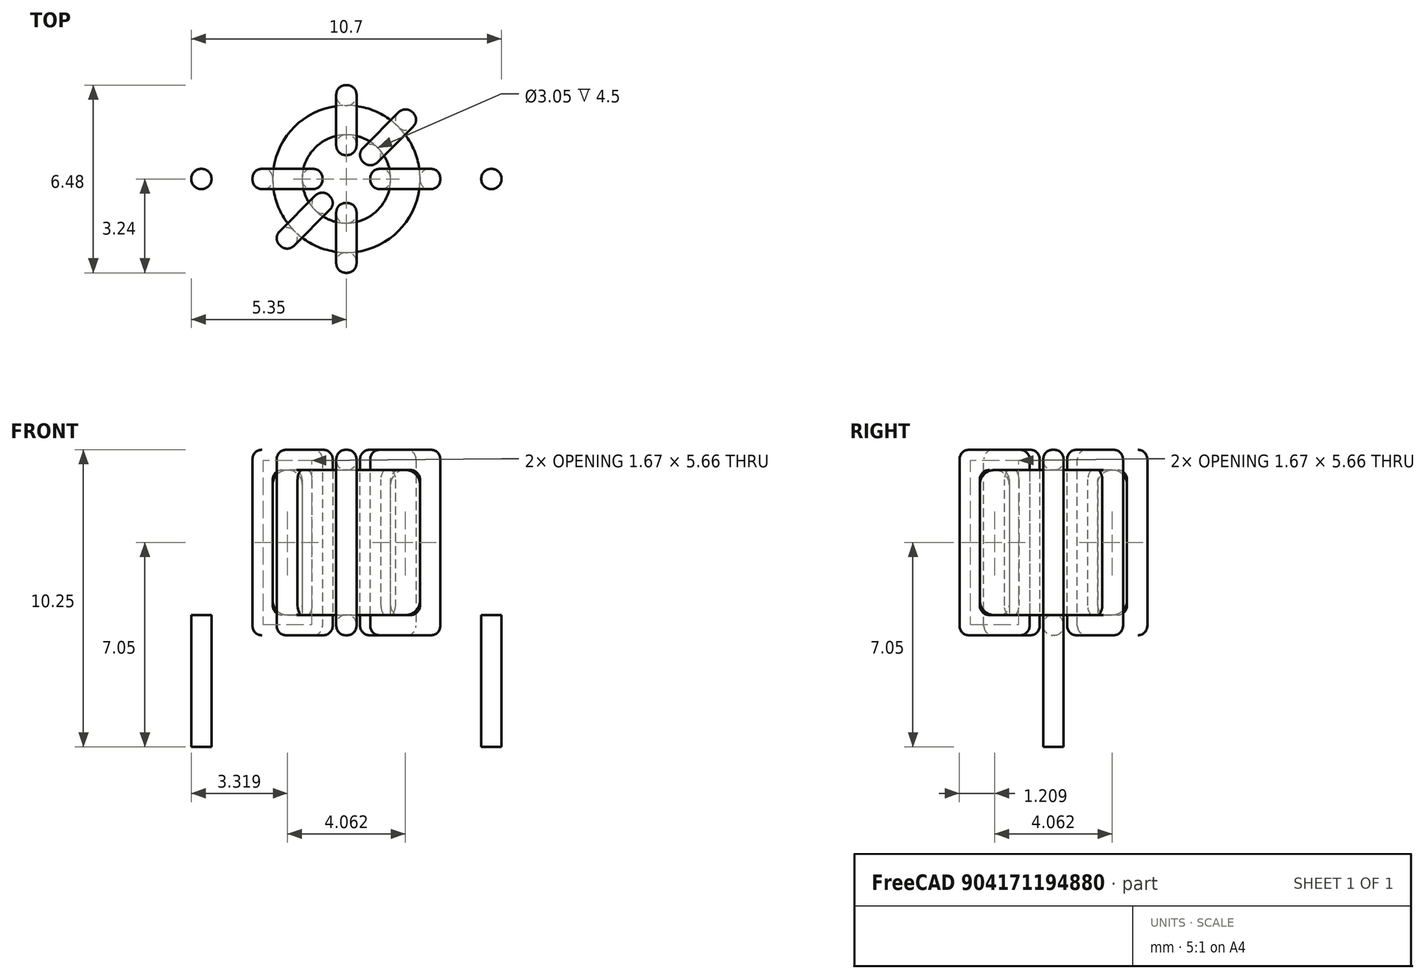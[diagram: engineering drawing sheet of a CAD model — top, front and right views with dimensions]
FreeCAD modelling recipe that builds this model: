
FCSTD DOCUMENT  (FreeCAD 0.16R6703 (Git))
Label: L_Toroid_Horizontal_D6.5mm_P10.00mm_Diameter7-5mm_Amidon-T25
License: All rights reserved
LicenseURL: http://en.wikipedia.org/wiki/All_rights_reserved
objects: Sketcher::SketchObject×6, PartDesign::Pad×6, PartDesign::Fillet×5, Spreadsheet::Sheet×1
note: 23 computed .brp shape members not serialized (recipe doc carries the construction recipe); baked Part::Feature solids carry a one-line shape summary decoded from their .brp

FEATURE [Spreadsheet::Sheet] Spreadsheet  label="dimensions"
  cells = A1=Wx; B1(Wx)=6.476999999999999; C1(WW)=3.048; D1=6.476999999999999; A2=Wy; B2(Wy)=6.476999999999999; D2=6.476999999999999; A3=RM; B3(RMx)=10; C3(RMy)=0; A4=d_wire; B4(d_wire)=0.7; A5=H; B5(H)=5; A6=offsetx; B6(offsetx)=-1.7615
FEATURE [Sketcher::SketchObject] Sketch
  Placement = pos=(0,0,1.2) rot=(0,0,1;0rad)
  expr: Placement.Base.z = 0.5 + Spreadsheet.d_wire
  expr: Constraints[0] = Spreadsheet.Wx / 2 - Spreadsheet.d_wire
  expr: Constraints[4] = Spreadsheet.WW / 2
  expr: Constraints[2] = Spreadsheet.RMy / 2
  expr: Constraints[1] = Spreadsheet.RMx / 2
  sketch-geometry (2):
    g0: Circle CenterX=5 CenterY=0 CenterZ=0 NormalX=0 NormalY=0 NormalZ=1 Radius=2.5385
    g1: Circle CenterX=5 CenterY=0 CenterZ=0 NormalX=0 NormalY=0 NormalZ=1 Radius=1.524
  constraints (5):
    c: Radius(g0) = 2.5385
    c: DistanceX(g-1,g0) = 5
    c: DistanceY(g-1,g0) = 0
    c: Coincident(g1,g0)
    c: Radius(g1) = 1.524
FEATURE [PartDesign::Pad] Pad
  Length = 5
  Length2 = 100
  Placement = pos=(0,0,1.2) rot=(0,0,1;0rad)
  Sketch = -> Sketch
  Type = 0
  expr: Length = Spreadsheet.H
FEATURE [Sketcher::SketchObject] Sketch001
  Placement = pos=(0,0,0.85) rot=(0,0,1;0rad)
  expr: Placement.Base.z = 0.5 + Spreadsheet.d_wire * 0.5
  expr: Constraints[4] = Spreadsheet.RMx
  expr: Constraints[2] = Spreadsheet.RMy
  expr: Constraints[1] = Spreadsheet.d_wire / 2
  sketch-geometry (2):
    g0: Circle CenterX=0 CenterY=0 CenterZ=0 NormalX=0 NormalY=0 NormalZ=1 Radius=0.35
    g1: Circle CenterX=10 CenterY=0 CenterZ=0 NormalX=0 NormalY=0 NormalZ=1 Radius=0.35
  constraints (5):
    c: Equal(g0,g1)
    c: Radius(g0) = 0.35
    c: DistanceY(g-1,g1) = 0
    c: Coincident(g0,g-1)
    c: DistanceX(g-1,g1) = 10
FEATURE [PartDesign::Pad] Pad001
  Length = 0.35
  Length2 = 4.2
  Placement = pos=(0,0,0.85) rot=(0,0,1;0rad)
  Reversed = true
  Sketch = -> Sketch001
  Type = 4
  expr: Length2 = 3.5 + Spreadsheet.d_wire
  expr: Length = Spreadsheet.d_wire / 2
FEATURE [PartDesign::Fillet] Fillet
  Base = -> Pad [Edge6,Edge3,Edge2]
  Placement = pos=(0,0,1.2) rot=(0,0,1;0rad)
  Radius = 0.5
FEATURE [Sketcher::SketchObject] Sketch003
  Placement = pos=(5,0,0) rot=(1,0,0;1.5708rad)
  expr: Placement.Base.x = Spreadsheet.RMx / 2
  expr: Constraints[49] = Spreadsheet.Wx - Spreadsheet.d_wire * 2
  expr: Constraints[44] = Spreadsheet.d_wire
  expr: Constraints[23] = Spreadsheet.H
  expr: Constraints[22] = Spreadsheet.Wx / 2 - Spreadsheet.d_wire
  expr: Placement.Base.y = Spreadsheet.RMy / 2
  expr: Constraints[21] = (Spreadsheet.Wx - Spreadsheet.WW) / 2 - Spreadsheet.d_wire
  expr: Constraints[19] = Spreadsheet.d_wire
  expr: Constraints[17] = Spreadsheet.d_wire
  expr: Constraints[18] = Spreadsheet.d_wire
  expr: Constraints[16] = Spreadsheet.d_wire
  sketch-geometry (16):
    g0: LineSegment StartX=-0.824 StartY=0.5 StartZ=0 EndX=-3.2385 EndY=0.5 EndZ=0
    g1: LineSegment StartX=-3.2385 StartY=0.5 StartZ=0 EndX=-3.2385 EndY=6.9 EndZ=0
    g2: LineSegment StartX=-3.2385 StartY=6.9 StartZ=0 EndX=-0.824 EndY=6.9 EndZ=0
    g3: LineSegment StartX=-0.824 StartY=6.9 StartZ=0 EndX=-0.824 EndY=0.5 EndZ=0
    g4: LineSegment StartX=-2.5385 StartY=6.2 StartZ=0 EndX=-1.524 EndY=6.2 EndZ=0
    g5: LineSegment StartX=-1.524 StartY=6.2 StartZ=0 EndX=-1.524 EndY=1.2 EndZ=0
    g6: LineSegment StartX=-1.524 StartY=1.2 StartZ=0 EndX=-2.5385 EndY=1.2 EndZ=0
    g7: LineSegment StartX=-2.5385 StartY=1.2 StartZ=0 EndX=-2.5385 EndY=6.2 EndZ=0
    g8: LineSegment StartX=0.824 StartY=6.9 StartZ=0 EndX=3.2385 EndY=6.9 EndZ=0
    g9: LineSegment StartX=3.2385 StartY=6.9 StartZ=0 EndX=3.2385 EndY=0.5 EndZ=0
    g10: LineSegment StartX=3.2385 StartY=0.5 StartZ=0 EndX=0.824 EndY=0.5 EndZ=0
    g11: LineSegment StartX=0.824 StartY=0.5 StartZ=0 EndX=0.824 EndY=6.9 EndZ=0
    g12: LineSegment StartX=1.524 StartY=6.2 StartZ=0 EndX=2.5385 EndY=6.2 EndZ=0
    g13: LineSegment StartX=2.5385 StartY=6.2 StartZ=0 EndX=2.5385 EndY=1.2 EndZ=0
    g14: LineSegment StartX=2.5385 StartY=1.2 StartZ=0 EndX=1.524 EndY=1.2 EndZ=0
    g15: LineSegment StartX=1.524 StartY=1.2 StartZ=0 EndX=1.524 EndY=6.2 EndZ=0
  constraints (50):
    c: Horizontal(g0)
    c: Coincident(g1,g0)
    c: Vertical(g1)
    c: Coincident(g2,g1)
    c: Horizontal(g2)
    c: Coincident(g3,g2)
    c: Coincident(g3,g0)
    c: Vertical(g3)
    c: Coincident(g4,g5)
    c: Coincident(g5,g6)
    c: Coincident(g6,g7)
    c: Coincident(g7,g4)
    c: Horizontal(g4)
    c: Horizontal(g6)
    c: Vertical(g5)
    c: Vertical(g7)
    c: DistanceX(g1,g4) = 0.7
    c: DistanceY(g4,g1) = 0.7
    c: DistanceX(g5,g0) = 0.7
    c: DistanceY(g0,g5) = 0.7
    c: DistanceY(g-1,g0) = 0.5
    c: DistanceX(g6,g6) = 1.0145
    c: DistanceX(g6,g-1) = 2.5385
    c: DistanceY(g7,g7) = 5
    c: Coincident(g8,g9)
    c: Coincident(g9,g10)
    c: Coincident(g10,g11)
    c: Coincident(g11,g8)
    c: Horizontal(g8)
    c: Horizontal(g10)
    c: Vertical(g9)
    c: Vertical(g11)
    c: Coincident(g12,g13)
    c: Coincident(g13,g14)
    c: Coincident(g14,g15)
    c: Coincident(g15,g12)
    c: Horizontal(g12)
    c: Horizontal(g14)
    c: Vertical(g13)
    c: Vertical(g15)
    c: DistanceY(g8,g2) = 0
    c: DistanceY(g10,g0) = 0
    c: DistanceY(g14,g5) = 0
    c: DistanceY(g12,g4) = 0
    c: DistanceX(g8,g12) = 0.7
    c: Equal(g8,g2)
    c: Equal(g12,g4)
    c: Equal(g9,g1)
    c: Equal(g13,g7)
    c: DistanceX(g4,g12) = 5.077
FEATURE [PartDesign::Pad] Pad002
  Length = 0.7
  Length2 = 100
  Midplane = true
  Placement = pos=(5,0,0) rot=(1,0,0;1.5708rad)
  Sketch = -> Sketch003
  Type = 0
  expr: Length = Spreadsheet.d_wire
FEATURE [PartDesign::Fillet] Fillet001
  Base = -> Pad002 [Edge38,Edge41,Edge42,Edge43,Edge29,Edge32,Edge33,Edge34,Edge25,Edge35,Edge36,Edge13,Edge14,Edge15,Edge16,Edge17,Edge18,Edge19,Edge1,Edge2,Edge3,Edge4,Edge5,Edge6,Edge7,Edge37,Edge39,Edge40,Edge20,Edge23,Edge24,Edge21,Edge22,Edge8,Edge9,Edge10,Edge11,Edge12,Edge26,Edge27,+8 more]
  Placement = pos=(5,0,0) rot=(1,0,0;1.5708rad)
  Radius = 0.329
  expr: Radius = Spreadsheet.d_wire * 0.47
FEATURE [Sketcher::SketchObject] Sketch004
  Placement = pos=(5,0,0) rot=(0.862856,0.357407,0.357407;1.71777rad)
  expr: Placement.Base.x = Spreadsheet.RMx / 2
  expr: Constraints[49] = Spreadsheet.Wx - 2 * Spreadsheet.d_wire
  expr: Constraints[44] = Spreadsheet.d_wire
  expr: Constraints[23] = Spreadsheet.H
  expr: Constraints[22] = Spreadsheet.Wx / 2 - Spreadsheet.d_wire
  expr: Placement.Base.y = Spreadsheet.RMy / 2
  expr: Constraints[21] = (Spreadsheet.Wx - Spreadsheet.WW) / 2 - Spreadsheet.d_wire
  expr: Constraints[19] = Spreadsheet.d_wire
  expr: Constraints[17] = Spreadsheet.d_wire
  expr: Constraints[18] = Spreadsheet.d_wire
  expr: Constraints[16] = Spreadsheet.d_wire
  sketch-geometry (16):
    g0: LineSegment StartX=-0.824 StartY=0.5 StartZ=0 EndX=-3.2385 EndY=0.5 EndZ=0
    g1: LineSegment StartX=-3.2385 StartY=0.5 StartZ=0 EndX=-3.2385 EndY=6.9 EndZ=0
    g2: LineSegment StartX=-3.2385 StartY=6.9 StartZ=0 EndX=-0.824 EndY=6.9 EndZ=0
    g3: LineSegment StartX=-0.824 StartY=6.9 StartZ=0 EndX=-0.824 EndY=0.5 EndZ=0
    g4: LineSegment StartX=-2.5385 StartY=6.2 StartZ=0 EndX=-1.524 EndY=6.2 EndZ=0
    g5: LineSegment StartX=-1.524 StartY=6.2 StartZ=0 EndX=-1.524 EndY=1.2 EndZ=0
    g6: LineSegment StartX=-1.524 StartY=1.2 StartZ=0 EndX=-2.5385 EndY=1.2 EndZ=0
    g7: LineSegment StartX=-2.5385 StartY=1.2 StartZ=0 EndX=-2.5385 EndY=6.2 EndZ=0
    g8: LineSegment StartX=0.824 StartY=6.9 StartZ=0 EndX=3.2385 EndY=6.9 EndZ=0
    g9: LineSegment StartX=3.2385 StartY=6.9 StartZ=0 EndX=3.2385 EndY=0.5 EndZ=0
    g10: LineSegment StartX=3.2385 StartY=0.5 StartZ=0 EndX=0.824 EndY=0.5 EndZ=0
    g11: LineSegment StartX=0.824 StartY=0.5 StartZ=0 EndX=0.824 EndY=6.9 EndZ=0
    g12: LineSegment StartX=1.524 StartY=6.2 StartZ=0 EndX=2.5385 EndY=6.2 EndZ=0
    g13: LineSegment StartX=2.5385 StartY=6.2 StartZ=0 EndX=2.5385 EndY=1.2 EndZ=0
    g14: LineSegment StartX=2.5385 StartY=1.2 StartZ=0 EndX=1.524 EndY=1.2 EndZ=0
    g15: LineSegment StartX=1.524 StartY=1.2 StartZ=0 EndX=1.524 EndY=6.2 EndZ=0
  constraints (50):
    c: Horizontal(g0)
    c: Coincident(g1,g0)
    c: Vertical(g1)
    c: Coincident(g2,g1)
    c: Horizontal(g2)
    c: Coincident(g3,g2)
    c: Coincident(g3,g0)
    c: Vertical(g3)
    c: Coincident(g4,g5)
    c: Coincident(g5,g6)
    c: Coincident(g6,g7)
    c: Coincident(g7,g4)
    c: Horizontal(g4)
    c: Horizontal(g6)
    c: Vertical(g5)
    c: Vertical(g7)
    c: DistanceX(g1,g4) = 0.7
    c: DistanceY(g4,g1) = 0.7
    c: DistanceX(g5,g0) = 0.7
    c: DistanceY(g0,g5) = 0.7
    c: DistanceY(g-1,g0) = 0.5
    c: DistanceX(g6,g6) = 1.0145
    c: DistanceX(g6,g-1) = 2.5385
    c: DistanceY(g7,g7) = 5
    c: Coincident(g8,g9)
    c: Coincident(g9,g10)
    c: Coincident(g10,g11)
    c: Coincident(g11,g8)
    c: Horizontal(g8)
    c: Horizontal(g10)
    c: Vertical(g9)
    c: Vertical(g11)
    c: Coincident(g12,g13)
    c: Coincident(g13,g14)
    c: Coincident(g14,g15)
    c: Coincident(g15,g12)
    c: Horizontal(g12)
    c: Horizontal(g14)
    c: Vertical(g13)
    c: Vertical(g15)
    c: DistanceY(g8,g2) = 0
    c: DistanceY(g10,g0) = 0
    c: DistanceY(g14,g5) = 0
    c: DistanceY(g12,g4) = 0
    c: DistanceX(g8,g12) = 0.7
    c: Equal(g8,g2)
    c: Equal(g12,g4)
    c: Equal(g9,g1)
    c: Equal(g13,g7)
    c: DistanceX(g4,g12) = 5.077
FEATURE [PartDesign::Pad] Pad003
  Length = 0.7
  Length2 = 100
  Midplane = true
  Placement = pos=(5,0,0) rot=(0.862856,0.357407,0.357407;1.71777rad)
  Sketch = -> Sketch004
  Type = 0
  expr: Length = Spreadsheet.d_wire
FEATURE [PartDesign::Fillet] Fillet002
  Base = -> Pad003 [Edge38,Edge41,Edge42,Edge43,Edge29,Edge32,Edge33,Edge34,Edge25,Edge35,Edge36,Edge13,Edge14,Edge15,Edge16,Edge17,Edge18,Edge19,Edge1,Edge2,Edge3,Edge4,Edge5,Edge6,Edge7,Edge37,Edge39,Edge40,Edge20,Edge23,Edge24,Edge21,Edge22,Edge8,Edge9,Edge10,Edge11,Edge12,Edge26,Edge27,+8 more]
  Placement = pos=(5,0,0) rot=(0.862856,0.357407,0.357407;1.71777rad)
  Radius = 0.329
  expr: Radius = Spreadsheet.d_wire * 0.47
FEATURE [Sketcher::SketchObject] Sketch005
  Placement = pos=(5,0,0) rot=(0.862856,-0.357407,-0.357407;1.71777rad)
  expr: Placement.Base.x = Spreadsheet.RMx / 2
  expr: Constraints[49] = Spreadsheet.Wx - 2 * Spreadsheet.d_wire
  expr: Constraints[44] = Spreadsheet.d_wire
  expr: Constraints[23] = Spreadsheet.H
  expr: Constraints[22] = Spreadsheet.Wx / 2 - Spreadsheet.d_wire
  expr: Placement.Base.y = Spreadsheet.RMy / 2
  expr: Constraints[21] = (Spreadsheet.Wx - Spreadsheet.WW) / 2 - Spreadsheet.d_wire
  expr: Constraints[19] = Spreadsheet.d_wire
  expr: Constraints[17] = Spreadsheet.d_wire
  expr: Constraints[18] = Spreadsheet.d_wire
  expr: Constraints[16] = Spreadsheet.d_wire
  sketch-geometry (16):
    g0: LineSegment StartX=-0.824 StartY=0.5 StartZ=0 EndX=-3.2385 EndY=0.5 EndZ=0
    g1: LineSegment StartX=-3.2385 StartY=0.5 StartZ=0 EndX=-3.2385 EndY=6.9 EndZ=0
    g2: LineSegment StartX=-3.2385 StartY=6.9 StartZ=0 EndX=-0.824 EndY=6.9 EndZ=0
    g3: LineSegment StartX=-0.824 StartY=6.9 StartZ=0 EndX=-0.824 EndY=0.5 EndZ=0
    g4: LineSegment StartX=-2.5385 StartY=6.2 StartZ=0 EndX=-1.524 EndY=6.2 EndZ=0
    g5: LineSegment StartX=-1.524 StartY=6.2 StartZ=0 EndX=-1.524 EndY=1.2 EndZ=0
    g6: LineSegment StartX=-1.524 StartY=1.2 StartZ=0 EndX=-2.5385 EndY=1.2 EndZ=0
    g7: LineSegment StartX=-2.5385 StartY=1.2 StartZ=0 EndX=-2.5385 EndY=6.2 EndZ=0
    g8: LineSegment StartX=0.824 StartY=6.9 StartZ=0 EndX=3.2385 EndY=6.9 EndZ=0
    g9: LineSegment StartX=3.2385 StartY=6.9 StartZ=0 EndX=3.2385 EndY=0.5 EndZ=0
    g10: LineSegment StartX=3.2385 StartY=0.5 StartZ=0 EndX=0.824 EndY=0.5 EndZ=0
    g11: LineSegment StartX=0.824 StartY=0.5 StartZ=0 EndX=0.824 EndY=6.9 EndZ=0
    g12: LineSegment StartX=1.524 StartY=6.2 StartZ=0 EndX=2.5385 EndY=6.2 EndZ=0
    g13: LineSegment StartX=2.5385 StartY=6.2 StartZ=0 EndX=2.5385 EndY=1.2 EndZ=0
    g14: LineSegment StartX=2.5385 StartY=1.2 StartZ=0 EndX=1.524 EndY=1.2 EndZ=0
    g15: LineSegment StartX=1.524 StartY=1.2 StartZ=0 EndX=1.524 EndY=6.2 EndZ=0
  constraints (50):
    c: Horizontal(g0)
    c: Coincident(g1,g0)
    c: Vertical(g1)
    c: Coincident(g2,g1)
    c: Horizontal(g2)
    c: Coincident(g3,g2)
    c: Coincident(g3,g0)
    c: Vertical(g3)
    c: Coincident(g4,g5)
    c: Coincident(g5,g6)
    c: Coincident(g6,g7)
    c: Coincident(g7,g4)
    c: Horizontal(g4)
    c: Horizontal(g6)
    c: Vertical(g5)
    c: Vertical(g7)
    c: DistanceX(g1,g4) = 0.7
    c: DistanceY(g4,g1) = 0.7
    c: DistanceX(g5,g0) = 0.7
    c: DistanceY(g0,g5) = 0.7
    c: DistanceY(g-1,g0) = 0.5
    c: DistanceX(g6,g6) = 1.0145
    c: DistanceX(g6,g-1) = 2.5385
    c: DistanceY(g7,g7) = 5
    c: Coincident(g8,g9)
    c: Coincident(g9,g10)
    c: Coincident(g10,g11)
    c: Coincident(g11,g8)
    c: Horizontal(g8)
    c: Horizontal(g10)
    c: Vertical(g9)
    c: Vertical(g11)
    c: Coincident(g12,g13)
    c: Coincident(g13,g14)
    c: Coincident(g14,g15)
    c: Coincident(g15,g12)
    c: Horizontal(g12)
    c: Horizontal(g14)
    c: Vertical(g13)
    c: Vertical(g15)
    c: DistanceY(g8,g2) = 0
    c: DistanceY(g10,g0) = 0
    c: DistanceY(g14,g5) = 0
    c: DistanceY(g12,g4) = 0
    c: DistanceX(g8,g12) = 0.7
    c: Equal(g8,g2)
    c: Equal(g12,g4)
    c: Equal(g9,g1)
    c: Equal(g13,g7)
    c: DistanceX(g4,g12) = 5.077
FEATURE [PartDesign::Pad] Pad004
  Length = 0.7
  Length2 = 100
  Midplane = true
  Placement = pos=(5,0,0) rot=(0.862856,-0.357407,-0.357407;1.71777rad)
  Sketch = -> Sketch005
  Type = 0
  expr: Length = Spreadsheet.d_wire
FEATURE [PartDesign::Fillet] Fillet003
  Base = -> Pad004 [Edge38,Edge41,Edge42,Edge43,Edge29,Edge32,Edge33,Edge34,Edge25,Edge35,Edge36,Edge13,Edge14,Edge15,Edge16,Edge17,Edge18,Edge19,Edge1,Edge2,Edge3,Edge4,Edge5,Edge6,Edge7,Edge37,Edge39,Edge40,Edge20,Edge23,Edge24,Edge21,Edge22,Edge8,Edge9,Edge10,Edge11,Edge12,Edge26,Edge27,+8 more]
  Placement = pos=(5,0,0) rot=(0.862856,-0.357407,-0.357407;1.71777rad)
  Radius = 0.329
  expr: Radius = Spreadsheet.d_wire * 0.47
FEATURE [Sketcher::SketchObject] Sketch006
  Placement = pos=(5,0,0) rot=(0.57735,0.57735,0.57735;2.0944rad)
  expr: Placement.Base.x = Spreadsheet.RMx / 2
  expr: Constraints[49] = Spreadsheet.Wx - Spreadsheet.d_wire * 2
  expr: Constraints[44] = Spreadsheet.d_wire
  expr: Constraints[23] = Spreadsheet.H
  expr: Constraints[22] = Spreadsheet.Wx / 2 - Spreadsheet.d_wire
  expr: Placement.Base.y = Spreadsheet.RMy / 2
  expr: Constraints[21] = (Spreadsheet.Wx - Spreadsheet.WW) / 2 - Spreadsheet.d_wire
  expr: Constraints[19] = Spreadsheet.d_wire
  expr: Constraints[17] = Spreadsheet.d_wire
  expr: Constraints[18] = Spreadsheet.d_wire
  expr: Constraints[16] = Spreadsheet.d_wire
  sketch-geometry (16):
    g0: LineSegment StartX=-0.824 StartY=0.5 StartZ=0 EndX=-3.2385 EndY=0.5 EndZ=0
    g1: LineSegment StartX=-3.2385 StartY=0.5 StartZ=0 EndX=-3.2385 EndY=6.9 EndZ=0
    g2: LineSegment StartX=-3.2385 StartY=6.9 StartZ=0 EndX=-0.824 EndY=6.9 EndZ=0
    g3: LineSegment StartX=-0.824 StartY=6.9 StartZ=0 EndX=-0.824 EndY=0.5 EndZ=0
    g4: LineSegment StartX=-2.5385 StartY=6.2 StartZ=0 EndX=-1.524 EndY=6.2 EndZ=0
    g5: LineSegment StartX=-1.524 StartY=6.2 StartZ=0 EndX=-1.524 EndY=1.2 EndZ=0
    g6: LineSegment StartX=-1.524 StartY=1.2 StartZ=0 EndX=-2.5385 EndY=1.2 EndZ=0
    g7: LineSegment StartX=-2.5385 StartY=1.2 StartZ=0 EndX=-2.5385 EndY=6.2 EndZ=0
    g8: LineSegment StartX=0.824 StartY=6.9 StartZ=0 EndX=3.2385 EndY=6.9 EndZ=0
    g9: LineSegment StartX=3.2385 StartY=6.9 StartZ=0 EndX=3.2385 EndY=0.5 EndZ=0
    g10: LineSegment StartX=3.2385 StartY=0.5 StartZ=0 EndX=0.824 EndY=0.5 EndZ=0
    g11: LineSegment StartX=0.824 StartY=0.5 StartZ=0 EndX=0.824 EndY=6.9 EndZ=0
    g12: LineSegment StartX=1.524 StartY=6.2 StartZ=0 EndX=2.5385 EndY=6.2 EndZ=0
    g13: LineSegment StartX=2.5385 StartY=6.2 StartZ=0 EndX=2.5385 EndY=1.2 EndZ=0
    g14: LineSegment StartX=2.5385 StartY=1.2 StartZ=0 EndX=1.524 EndY=1.2 EndZ=0
    g15: LineSegment StartX=1.524 StartY=1.2 StartZ=0 EndX=1.524 EndY=6.2 EndZ=0
  constraints (50):
    c: Horizontal(g0)
    c: Coincident(g1,g0)
    c: Vertical(g1)
    c: Coincident(g2,g1)
    c: Horizontal(g2)
    c: Coincident(g3,g2)
    c: Coincident(g3,g0)
    c: Vertical(g3)
    c: Coincident(g4,g5)
    c: Coincident(g5,g6)
    c: Coincident(g6,g7)
    c: Coincident(g7,g4)
    c: Horizontal(g4)
    c: Horizontal(g6)
    c: Vertical(g5)
    c: Vertical(g7)
    c: DistanceX(g1,g4) = 0.7
    c: DistanceY(g4,g1) = 0.7
    c: DistanceX(g5,g0) = 0.7
    c: DistanceY(g0,g5) = 0.7
    c: DistanceY(g-1,g0) = 0.5
    c: DistanceX(g6,g6) = 1.0145
    c: DistanceX(g6,g-1) = 2.5385
    c: DistanceY(g7,g7) = 5
    c: Coincident(g8,g9)
    c: Coincident(g9,g10)
    c: Coincident(g10,g11)
    c: Coincident(g11,g8)
    c: Horizontal(g8)
    c: Horizontal(g10)
    c: Vertical(g9)
    c: Vertical(g11)
    c: Coincident(g12,g13)
    c: Coincident(g13,g14)
    c: Coincident(g14,g15)
    c: Coincident(g15,g12)
    c: Horizontal(g12)
    c: Horizontal(g14)
    c: Vertical(g13)
    c: Vertical(g15)
    c: DistanceY(g8,g2) = 0
    c: DistanceY(g10,g0) = 0
    c: DistanceY(g14,g5) = 0
    c: DistanceY(g12,g4) = 0
    c: DistanceX(g8,g12) = 0.7
    c: Equal(g8,g2)
    c: Equal(g12,g4)
    c: Equal(g9,g1)
    c: Equal(g13,g7)
    c: DistanceX(g4,g12) = 5.077
FEATURE [PartDesign::Pad] Pad005
  Length = 0.7
  Length2 = 100
  Midplane = true
  Placement = pos=(5,0,0) rot=(0.57735,0.57735,0.57735;2.0944rad)
  Sketch = -> Sketch006
  Type = 0
  expr: Length = Spreadsheet.d_wire
FEATURE [PartDesign::Fillet] Fillet004
  Base = -> Pad005 [Edge38,Edge41,Edge42,Edge43,Edge29,Edge32,Edge33,Edge34,Edge25,Edge35,Edge36,Edge13,Edge14,Edge15,Edge16,Edge17,Edge18,Edge19,Edge1,Edge2,Edge3,Edge4,Edge5,Edge6,Edge7,Edge37,Edge39,Edge40,Edge20,Edge23,Edge24,Edge21,Edge22,Edge8,Edge9,Edge10,Edge11,Edge12,Edge26,Edge27,+8 more]
  Placement = pos=(5,0,0) rot=(0.57735,0.57735,0.57735;2.0944rad)
  Radius = 0.329
  expr: Radius = Spreadsheet.d_wire * 0.47
